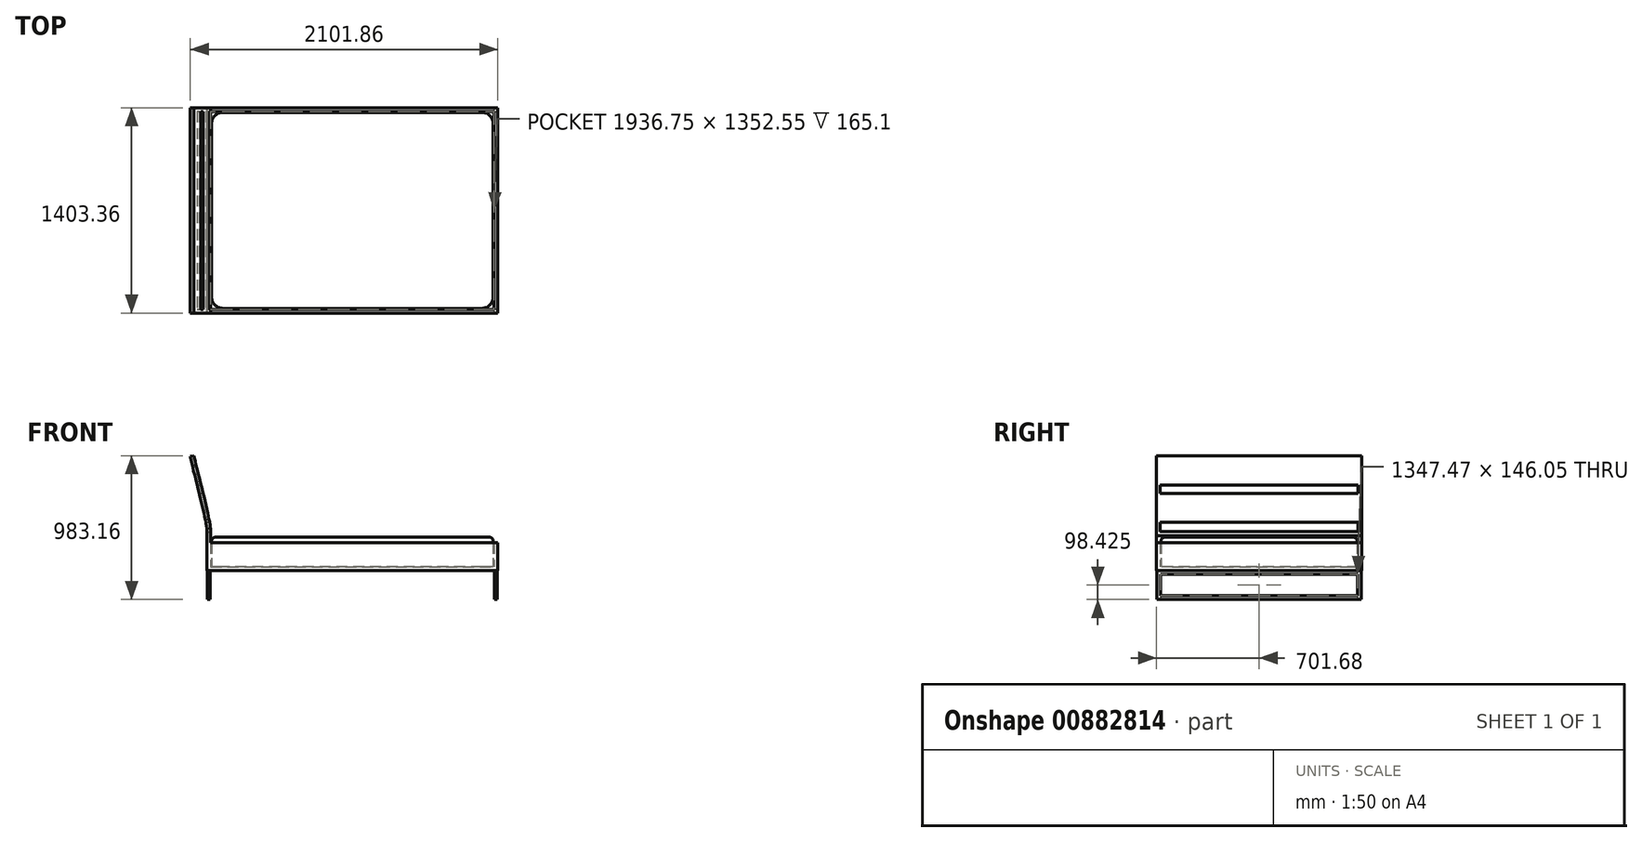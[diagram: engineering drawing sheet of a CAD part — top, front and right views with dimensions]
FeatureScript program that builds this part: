
annotation { "Feature Type Name" : "Feature", "Feature Type Description" : "" }
export const myFeature = defineFeature(function(context is Context, id is Id, definition is map)
    precondition{}
    {
        {
            var Q0;
            Q0=qCreatedBy(makeId("Top.planeOp"),FACE);
            var sketch = newSketch(context, id + "F0", { "sketchPlane" : qUnion([Q0])});
            skLineSegment(sketch, "E0.bottom", {"start": v(993.78, -701.67) * mm, "end": v(-993.78, -701.68) * mm});
            skLineSegment(sketch, "E0.top", {"start": v(993.78, 701.68) * mm, "end": v(-993.78, 701.67) * mm});
            skLineSegment(sketch, "E0.left", {"start": v(993.78, -701.67) * mm, "end": v(993.78, 701.68) * mm});
            skLineSegment(sketch, "E0.right", {"start": v(-993.78, -701.68) * mm, "end": v(-993.77, 701.67) * mm});
            skPoint(sketch, "E0.middle", {"position": v(0, 0) * mm});
            skLineSegment(sketch, "E1.0", {"start": v(968.38, -676.27) * mm, "end": v(968.38, 676.27) * mm});
            skLineSegment(sketch, "E1.1", {"start": v(968.38, -676.27) * mm, "end": v(-968.38, -676.28) * mm});
            skLineSegment(sketch, "E1.2", {"start": v(-968.38, -676.28) * mm, "end": v(-968.37, 676.27) * mm});
            skLineSegment(sketch, "E1.3", {"start": v(968.38, 676.28) * mm, "end": v(-968.37, 676.27) * mm});
            skSolve(sketch);
        }
        {
            var Q0;
            Q0=makeQuery(id+"F0.imprint","IMPRINT",FACE,{"disambiguationData":[TD([[makeQuery(id+"F0.imprint","IMPRINT",EDGE,{"derivedFrom":sQuery(id+"F0.wireOp",EDGE,"E0.bottom")}),-1.0]])]});
            extrude(context, id + "F1", {"entities" : qUnion([Q0]), "depth" : 190.5 * mm, "offsetDistance" : 25.4 * mm});
        }
        {
            var Q0;
            Q0=makeQuery(id+"F1.opExtrude","CAP_FACE",FACE,{"disambiguationData":[OSD([sQuery(id+"F0.wireOp",EDGE,"E0.bottom"),sQuery(id+"F0.wireOp",EDGE,"E0.top"),sQuery(id+"F0.wireOp",EDGE,"E0.left"),sQuery(id+"F0.wireOp",EDGE,"E0.right"),sQuery(id+"F0.wireOp",EDGE,"E1.0"),sQuery(id+"F0.wireOp",EDGE,"E1.1"),sQuery(id+"F0.wireOp",EDGE,"E1.2"),sQuery(id+"F0.wireOp",EDGE,"E1.3")])],"isStart":true});
            var sketch = newSketch(context, id + "F2", { "sketchPlane" : qUnion([Q0])});
            skLineSegment(sketch, "E2.0", {"start": v(991.24, 699.13) * mm, "end": v(991.24, -699.14) * mm});
            skLineSegment(sketch, "E2.1", {"start": v(991.24, 699.13) * mm, "end": v(970.91, 699.13) * mm});
            skLineSegment(sketch, "E2.2", {"start": v(970.91, 699.13) * mm, "end": v(970.92, -699.14) * mm});
            skLineSegment(sketch, "E2.3", {"start": v(991.24, -699.14) * mm, "end": v(970.92, -699.14) * mm});
            skLineSegment(sketch, "E3", {"start": v(0, 701.68) * mm, "end": v(0, -866.46) * mm});
            skPoint(sketch, "E3.endSnap0", {"position": v(0, -701.68) * mm});
            skLineSegment(sketch, "E4.MirrorCS", {"start": v(-991.24, 699.13) * mm, "end": v(-970.91, 699.13) * mm});
            skLineSegment(sketch, "E5.MirrorCS", {"start": v(-991.24, -699.14) * mm, "end": v(-970.92, -699.14) * mm});
            skLineSegment(sketch, "E6.MirrorCS", {"start": v(-970.91, 699.13) * mm, "end": v(-970.92, -699.14) * mm});
            skLineSegment(sketch, "E7.MirrorCS", {"start": v(-991.24, 699.13) * mm, "end": v(-991.24, -699.14) * mm});
            skSolve(sketch);
        }
        {
            var Q0;
            Q0 = qSketchRegion(id + "F2", true);
            extrude(context, id + "F3", {"entities" : qUnion([Q0]), "operationType" : NewBodyOperationType.ADD, "depth" : 196.85 * mm, "offsetDistance" : 25.4 * mm});
        }
        {
            var Q0;
            Q0=makeQuery(id+"F3.opExtrude","SWEPT_FACE",FACE,{"disambiguationData":[OSD([sQuery(id+"F2.wireOp",EDGE,"E2.0")])]});
            var sketch = newSketch(context, id + "F4", { "sketchPlane" : qUnion([Q0])});
            skLineSegment(sketch, "E8.bottom", {"start": v(-699.13, 0) * mm, "end": v(699.14, 0) * mm});
            skLineSegment(sketch, "E8.top", {"start": v(-699.13, -196.85) * mm, "end": v(699.14, -196.85) * mm});
            skLineSegment(sketch, "E8.left", {"start": v(-699.13, 0) * mm, "end": v(-699.13, -196.85) * mm});
            skLineSegment(sketch, "E8.right", {"start": v(699.14, 0) * mm, "end": v(699.14, -196.85) * mm});
            skLineSegment(sketch, "E9.0", {"start": v(-673.73, -25.4) * mm, "end": v(673.74, -25.4) * mm});
            skLineSegment(sketch, "E9.1", {"start": v(-673.73, -25.4) * mm, "end": v(-673.73, -171.45) * mm});
            skLineSegment(sketch, "E9.2", {"start": v(-673.73, -171.45) * mm, "end": v(673.74, -171.45) * mm});
            skLineSegment(sketch, "E9.3", {"start": v(673.74, -25.4) * mm, "end": v(673.74, -171.45) * mm});
            skSolve(sketch);
        }
        {
            var Q0;
            Q0=makeQuery(id+"F4.imprint","IMPRINT",FACE,{"disambiguationData":[TD([[makeQuery(id+"F4.imprint","IMPRINT",EDGE,{"derivedFrom":sQuery(id+"F4.wireOp",EDGE,"E9.0")}),-1.0]])]});
            extrude(context, id + "F5", {"entities" : qUnion([Q0]), "operationType" : NewBodyOperationType.REMOVE, "oppositeDirection" : true, "depth" : 2369.82 * mm, "offsetDistance" : 25.4 * mm});
        }
        {
            var Q0;
            Q0=makeQuery(id+"F5.boolean.opBoolean","COPY",FACE,{"disambiguationData":[TD([makeQuery(id+"F3.opExtrude","SWEPT_FACE",FACE,{"disambiguationData":[OSD([sQuery(id+"F2.wireOp",EDGE,"E6.MirrorCS")])]})])],"derivedFrom":makeQuery(id+"F5.opExtrude","SWEPT_FACE",FACE,{"disambiguationData":[OSD([sQuery(id+"F4.wireOp",EDGE,"E9.2")])]})});
            var sketch = newSketch(context, id + "F6", { "sketchPlane" : qUnion([Q0])});
            skLineSegment(sketch, "E10.bottom", {"start": v(-970.91, 673.74) * mm, "end": v(-991.24, 673.74) * mm});
            skLineSegment(sketch, "E10.top", {"start": v(-970.91, -673.73) * mm, "end": v(-991.24, -673.73) * mm});
            skLineSegment(sketch, "E10.left", {"start": v(-970.91, 673.74) * mm, "end": v(-970.91, -673.73) * mm});
            skLineSegment(sketch, "E10.right", {"start": v(-991.24, 673.74) * mm, "end": v(-991.24, -673.73) * mm});
            skSolve(sketch);
        }
        {
            var Q0;
            Q0=makeQuery(id+"F6.imprint","IMPRINT",FACE,{"disambiguationData":[TD([[makeQuery(id+"F6.imprint","IMPRINT",EDGE,{"derivedFrom":sQuery(id+"F6.wireOp",EDGE,"E10.bottom")}),-1.0]])]});
            extrude(context, id + "F7", {"entities" : qUnion([Q0]), "operationType" : NewBodyOperationType.REMOVE, "oppositeDirection" : true, "depth" : 55.88 * mm, "offsetDistance" : 25.4 * mm});
        }
        {
            var Q0;
            Q0=makeQuery(id+"F1.opExtrude","CAP_FACE",FACE,{"disambiguationData":[OSD([sQuery(id+"F0.wireOp",EDGE,"E0.bottom"),sQuery(id+"F0.wireOp",EDGE,"E0.top"),sQuery(id+"F0.wireOp",EDGE,"E0.left"),sQuery(id+"F0.wireOp",EDGE,"E0.right"),sQuery(id+"F0.wireOp",EDGE,"E1.0"),sQuery(id+"F0.wireOp",EDGE,"E1.1"),sQuery(id+"F0.wireOp",EDGE,"E1.2"),sQuery(id+"F0.wireOp",EDGE,"E1.3")])],"isStart":true});
            var sketch = newSketch(context, id + "F8", { "sketchPlane" : qUnion([Q0])});
            skLineSegment(sketch, "E11.bottom", {"start": v(-991.24, 699.13) * mm, "end": v(991.24, 699.13) * mm});
            skLineSegment(sketch, "E11.top", {"start": v(-991.24, -699.13) * mm, "end": v(991.24, -699.13) * mm});
            skLineSegment(sketch, "E11.left", {"start": v(-991.24, 699.13) * mm, "end": v(-991.24, -699.13) * mm});
            skLineSegment(sketch, "E11.right", {"start": v(991.24, 699.13) * mm, "end": v(991.24, -699.13) * mm});
            skPoint(sketch, "E11.middle", {"position": v(0, 0) * mm});
            skSolve(sketch);
        }
        {
            var Q0;
            Q0=makeQuery(id+"F8.imprint","IMPRINT",FACE,{"disambiguationData":[TD([[makeQuery(id+"F8.imprint","IMPRINT",EDGE,{"derivedFrom":sQuery(id+"F8.wireOp",EDGE,"0xnUU2Pv-F16W-MBvP-qyod-82M0PbmJ6Gg6.bottom")}),1.0]])]});
            var Q1;
            Q1=makeQuery(id+"F8.imprint","IMPRINT",FACE,{"disambiguationData":[TD([[makeQuery(id+"F8.imprint","IMPRINT",EDGE,{"derivedFrom":makeQuery(id+"F1.opExtrude","CAP_EDGE",EDGE,{"disambiguationData":[OSD([sQuery(id+"F0.wireOp",EDGE,"E1.0")])],"isStart":true})}),-1.0]])]});
            extrude(context, id + "F9", {"entities" : qUnion([Q0, Q1]), "oppositeDirection" : true, "depth" : 25.4 * mm, "offsetDistance" : 25.4 * mm});
        }
        {
            var Q0;
            Q0=makeQuery(id+"F1.opExtrude","SWEPT_FACE",FACE,{"disambiguationData":[OSD([sQuery(id+"F0.wireOp",EDGE,"E0.bottom")])]});
            var sketch = newSketch(context, id + "F10", { "sketchPlane" : qUnion([Q0])});
            skLineSegment(sketch, "E12", {"start": v(-993.78, 190.5) * mm, "end": v(-993.78, 241.3) * mm});
            skFitSpline(sketch, "E13", {"points": [v(-993.78, 241.3) * mm, v(-1108.08, 781.05) * mm], "startDerivative": vector(16.2, 298.55) * mm, "endDerivative": vector(-114.3, 539.75) * mm});
            skFitSpline(sketch, "E14.0", {"points": [v(-968.41, 239.92) * mm, v(-968.22, 243.54) * mm, v(-968.03, 250.97) * mm, v(-968.38, 266.66) * mm, v(-970.03, 287.91) * mm, v(-973.69, 316) * mm, v(-978.8, 346.5) * mm, v(-985.16, 379.14) * mm, v(-995.06, 425.14) * mm, v(-1009.61, 486.49) * mm, v(-1029.05, 563.58) * mm, v(-1048.93, 641.37) * mm, v(-1067.74, 717.03) * mm, v(-1078.53, 764.11) * mm, v(-1083.23, 786.31) * mm]});
            skLineSegment(sketch, "E15", {"start": v(-1108.08, 781.05) * mm, "end": v(-1083.23, 786.31) * mm});
            skLineSegment(sketch, "E16", {"start": v(-993.78, 190.5) * mm, "end": v(-968.38, 190.5) * mm});
            skLineSegment(sketch, "E17", {"start": v(-968.38, 190.5) * mm, "end": v(-968.41, 239.92) * mm});
            skSolve(sketch);
        }
        {
            var Q0;
            Q0=makeQuery(id+"F10.imprint","IMPRINT",FACE,{"disambiguationData":[TD([[makeQuery(id+"F10.imprint","IMPRINT",EDGE,{"derivedFrom":sQuery(id+"F10.wireOp",EDGE,"E12")}),-1.0]])]});
            var Q1;
            Q1=makeQuery(id+"F1.opExtrude","SWEPT_FACE",FACE,{"disambiguationData":[OSD([sQuery(id+"F0.wireOp",EDGE,"E0.top")])]});
            extrude(context, id + "F11", {"entities" : qUnion([Q0]), "operationType" : NewBodyOperationType.ADD, "endBound" : BoundingType.UP_TO_SURFACE, "oppositeDirection" : true, "depth" : 1247.14 * mm, "endBoundEntityFace" : qUnion([Q1]), "offsetDistance" : 25.4 * mm});
        }
        {
            var Q0;
            Q0=makeQuery(id+"F11.opExtrude","SWEPT_FACE",FACE,{"disambiguationData":[OSD([sQuery(id+"F10.wireOp",EDGE,"E17")])]});
            var sketch = newSketch(context, id + "F12", { "sketchPlane" : qUnion([Q0])});
            skLineSegment(sketch, "E18.1", {"start": v(-676.28, 266.05) * mm, "end": v(676.28, 266.05) * mm});
            skLineSegment(sketch, "E19.bottom", {"start": v(676.28, 330.93) * mm, "end": v(-676.28, 330.93) * mm});
            skPoint(sketch, "E19.middle", {"position": v(0, 261.08) * mm});
            skLineSegment(sketch, "E20.bottom", {"start": v(-676.28, 527.78) * mm, "end": v(676.28, 527.78) * mm});
            skLineSegment(sketch, "E20.top", {"start": v(-676.28, 584.93) * mm, "end": v(676.28, 584.93) * mm});
            skLineSegment(sketch, "E20.left", {"start": v(-676.28, 527.78) * mm, "end": v(-676.28, 584.93) * mm});
            skLineSegment(sketch, "E20.right", {"start": v(676.28, 527.78) * mm, "end": v(676.28, 584.93) * mm});
            skPoint(sketch, "E20.middle", {"position": v(0, 556.36) * mm});
            skLineSegment(sketch, "E21", {"start": v(-676.28, 266.05) * mm, "end": v(-676.28, 330.93) * mm});
            skLineSegment(sketch, "E22", {"start": v(676.28, 266.05) * mm, "end": v(676.28, 330.93) * mm});
            skSolve(sketch);
        }
        {
            var Q0;
            Q0=makeQuery(id+"F12.imprint","IMPRINT",FACE,{"disambiguationData":[TD([[makeQuery(id+"F12.imprint","IMPRINT",EDGE,{"derivedFrom":sQuery(id+"F12.wireOp",EDGE,"E20.bottom")}),1.0]])]});
            var Q1;
            Q1=makeQuery(id+"F12.imprint","IMPRINT",FACE,{"disambiguationData":[TD([[makeQuery(id+"F12.imprint","IMPRINT",EDGE,{"derivedFrom":sQuery(id+"F12.wireOp",EDGE,"E18.1")}),1.0]])]});
            extrude(context, id + "F13", {"entities" : qUnion([Q0, Q1]), "operationType" : NewBodyOperationType.REMOVE, "oppositeDirection" : true, "depth" : 226.06 * mm, "offsetDistance" : 25.4 * mm});
        }
        {
            var Q0;
            Q0=makeQuery(id+"F9.opExtrude","SWEPT_BODY",BODY,{"disambiguationData":[OSD([sQuery(id+"F0.wireOp",EDGE,"E1.0"),sQuery(id+"F0.wireOp",EDGE,"E1.1"),sQuery(id+"F0.wireOp",EDGE,"E1.2"),sQuery(id+"F0.wireOp",EDGE,"E1.3")])]});
            deleteBodies(context, id + "F14", {"entities" : qUnion([Q0])});
        }
        {
            var Q0;
            Q0=makeQuery(id+"F1.opExtrude","CAP_FACE",FACE,{"disambiguationData":[OSD([sQuery(id+"F0.wireOp",EDGE,"E0.bottom"),sQuery(id+"F0.wireOp",EDGE,"E0.top"),sQuery(id+"F0.wireOp",EDGE,"E0.left"),sQuery(id+"F0.wireOp",EDGE,"E0.right"),sQuery(id+"F0.wireOp",EDGE,"E1.0"),sQuery(id+"F0.wireOp",EDGE,"E1.1"),sQuery(id+"F0.wireOp",EDGE,"E1.2"),sQuery(id+"F0.wireOp",EDGE,"E1.3")])],"isStart":true});
            var sketch = newSketch(context, id + "F15", { "sketchPlane" : qUnion([Q0])});
            skLineSegment(sketch, "E23.bottom", {"start": v(991.24, -699.14) * mm, "end": v(-993.78, -699.14) * mm});
            skLineSegment(sketch, "E23.top", {"start": v(991.24, 701.68) * mm, "end": v(-993.78, 701.68) * mm});
            skLineSegment(sketch, "E23.left", {"start": v(991.24, -699.14) * mm, "end": v(991.24, 701.68) * mm});
            skLineSegment(sketch, "E23.right", {"start": v(-993.78, -699.14) * mm, "end": v(-993.78, 701.68) * mm});
            skSolve(sketch);
        }
        {
            var Q0;
            Q0=makeQuery(id+"F15.imprint","IMPRINT",FACE,{"disambiguationData":[TD([[makeQuery(id+"F15.imprint","IMPRINT",EDGE,{"derivedFrom":makeQuery(id+"F1.opExtrude","CAP_EDGE",EDGE,{"disambiguationData":[OSD([sQuery(id+"F0.wireOp",EDGE,"E1.0")])],"isStart":true})}),-1.0]])]});
            var Q1;
            {var subQ6=sQuery(id+"F15.wireOp",EDGE,"E23.top");Q1=makeQuery(id+"F15.imprint","IMPRINT",FACE,{"disambiguationData":[TD([[makeQuery(id+"F15.imprint","IMPRINT",EDGE,{"derivedFrom":subQ6}),1.0]])]});}
            extrude(context, id + "F16", {"entities" : qUnion([Q0, Q1]), "operationType" : NewBodyOperationType.ADD, "oppositeDirection" : true, "depth" : 25.4 * mm, "offsetDistance" : 25.4 * mm});
        }
        {
            var Q0;
            Q0=makeQuery(id+"F16.opExtrude","CAP_FACE",FACE,{"disambiguationData":[OSD([sQuery(id+"F2.wireOp",EDGE,"E2.1"),sQuery(id+"F2.wireOp",EDGE,"E2.2"),sQuery(id+"F2.wireOp",EDGE,"E4.MirrorCS"),sQuery(id+"F2.wireOp",EDGE,"E6.MirrorCS"),sQuery(id+"F2.wireOp",EDGE,"E7.MirrorCS"),sQuery(id+"F15.wireOp",EDGE,"E23.bottom"),sQuery(id+"F15.wireOp",EDGE,"E23.top"),sQuery(id+"F15.wireOp",EDGE,"E23.left"),sQuery(id+"F15.wireOp",EDGE,"E23.right")])],"isStart":false});
            var sketch = newSketch(context, id + "F17", { "sketchPlane" : qUnion([Q0])});
            skLineSegment(sketch, "E24.0", {"start": v(885.82, 669.92) * mm, "end": v(-885.82, 669.92) * mm});
            skLineSegment(sketch, "E24.1", {"start": v(962.02, -593.72) * mm, "end": v(962.02, 593.72) * mm});
            skLineSegment(sketch, "E24.2", {"start": v(885.82, -669.92) * mm, "end": v(-885.82, -669.92) * mm});
            skLineSegment(sketch, "E24.3", {"start": v(-962.02, -593.72) * mm, "end": v(-962.02, 593.72) * mm});
            skPoint(sketch, "E25.visualSharp", {"position": v(-962.02, 669.92) * mm});
            skArc(sketch, "E25.filletArc", {"start": v(-885.82, 669.92) * mm, "mid": v(-939.7, 647.6) * mm, "end": v(-962.02, 593.72) * mm});
            skPoint(sketch, "E26.visualSharp", {"position": v(962.02, 669.92) * mm});
            skArc(sketch, "E26.filletArc", {"start": v(962.02, 593.72) * mm, "mid": v(939.7, 647.6) * mm, "end": v(885.82, 669.92) * mm});
            skPoint(sketch, "E27.visualSharp", {"position": v(962.02, -669.92) * mm});
            skArc(sketch, "E27.filletArc", {"start": v(885.82, -669.92) * mm, "mid": v(939.7, -647.6) * mm, "end": v(962.02, -593.72) * mm});
            skPoint(sketch, "E28.visualSharp", {"position": v(-962.02, -669.92) * mm});
            skArc(sketch, "E28.filletArc", {"start": v(-962.02, -593.72) * mm, "mid": v(-939.7, -647.6) * mm, "end": v(-885.82, -669.92) * mm});
            skSolve(sketch);
        }
        {
            var Q0;
            Q0=makeQuery(id+"F17.imprint","IMPRINT",FACE,{"disambiguationData":[TD([[makeQuery(id+"F17.imprint","IMPRINT",EDGE,{"derivedFrom":sQuery(id+"F17.wireOp",EDGE,"E24.0")}),1.0]])]});
            extrude(context, id + "F18", {"entities" : qUnion([Q0]), "flatOperationType" : FlatOperationType.REMOVE, "depth" : 203.2 * mm, "offsetDistance" : 25.4 * mm, "domain" : OperationDomain.MODEL});
        }
        {
            var Q0;
            Q0=makeQuery(id+"F18.opExtrude","CAP_FACE",FACE,{"disambiguationData":[OSD([sQuery(id+"F17.wireOp",EDGE,"E24.0"),sQuery(id+"F17.wireOp",EDGE,"E24.1"),sQuery(id+"F17.wireOp",EDGE,"E24.2"),sQuery(id+"F17.wireOp",EDGE,"E24.3"),sQuery(id+"F17.wireOp",EDGE,"E25.filletArc"),sQuery(id+"F17.wireOp",EDGE,"E26.filletArc"),sQuery(id+"F17.wireOp",EDGE,"E27.filletArc"),sQuery(id+"F17.wireOp",EDGE,"E28.filletArc")])],"isStart":false});
            fillet(context, id + "F19", {"entities" : qUnion([Q0]), "radius" : 25.4 * mm, "tangentPropagation" : true, "allowEdgeOverflow" : false});
        }
    });
